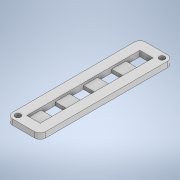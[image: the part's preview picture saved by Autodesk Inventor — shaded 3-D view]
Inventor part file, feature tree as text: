
AUTODESK INVENTOR PART (.ipt)
format: ipt  version: 2020 (Build 240168000, 168)  size: 155,648 bytes
history: native  units: mm
features: sketch x4, extrude x3, fillet x1, hole x1
ambient origin geometry x8: Origin, YZ Plane, XZ Plane, XY Plane, X Axis, Y Axis, Z Axis, Center Point
bodies: Solid1 (feature_tree)
feature tree (9):
  extrude  "Extrusion1"  Depth=120.0mm
  extrude  "Extrusion2"  Depth=12.0mm
  extrude  "Extrusion3"  Depth=2.0mm TaperAngle=0.0deg
  fillet  "Fillet1"  Radius=12.75mm
  hole  "Hole1"  [1 undecoded]
  sketch  "Sketch1"  dims[d0=30.0mm d1=120.0mm]
  sketch  "Sketch2"  dims[d2=5.0mm d3=0.0mm d4=12.0mm]
  sketch  "Sketch3"  dims[d5=102.0mm d7=2.0mm d8=0.0mm d9=12.75mm]
  sketch  "Sketch4"  dims[d10=12.75mm d11=40.0mm d13=25.5mm d14=10.0mm d16=10.0mm d18=2.0mm d19=0.0mm d20=5.0mm d21=3.0mm d22=6.0mm d23=5.0mm d24=2.0mm d25=90.0deg d26=8.0mm d27=20.594885mm]
note: 1 required parameter value undecoded (feature->parameter linkage not recoverable at this tier; creation-order binding heuristic only, values carry confidence <= 0.55)
